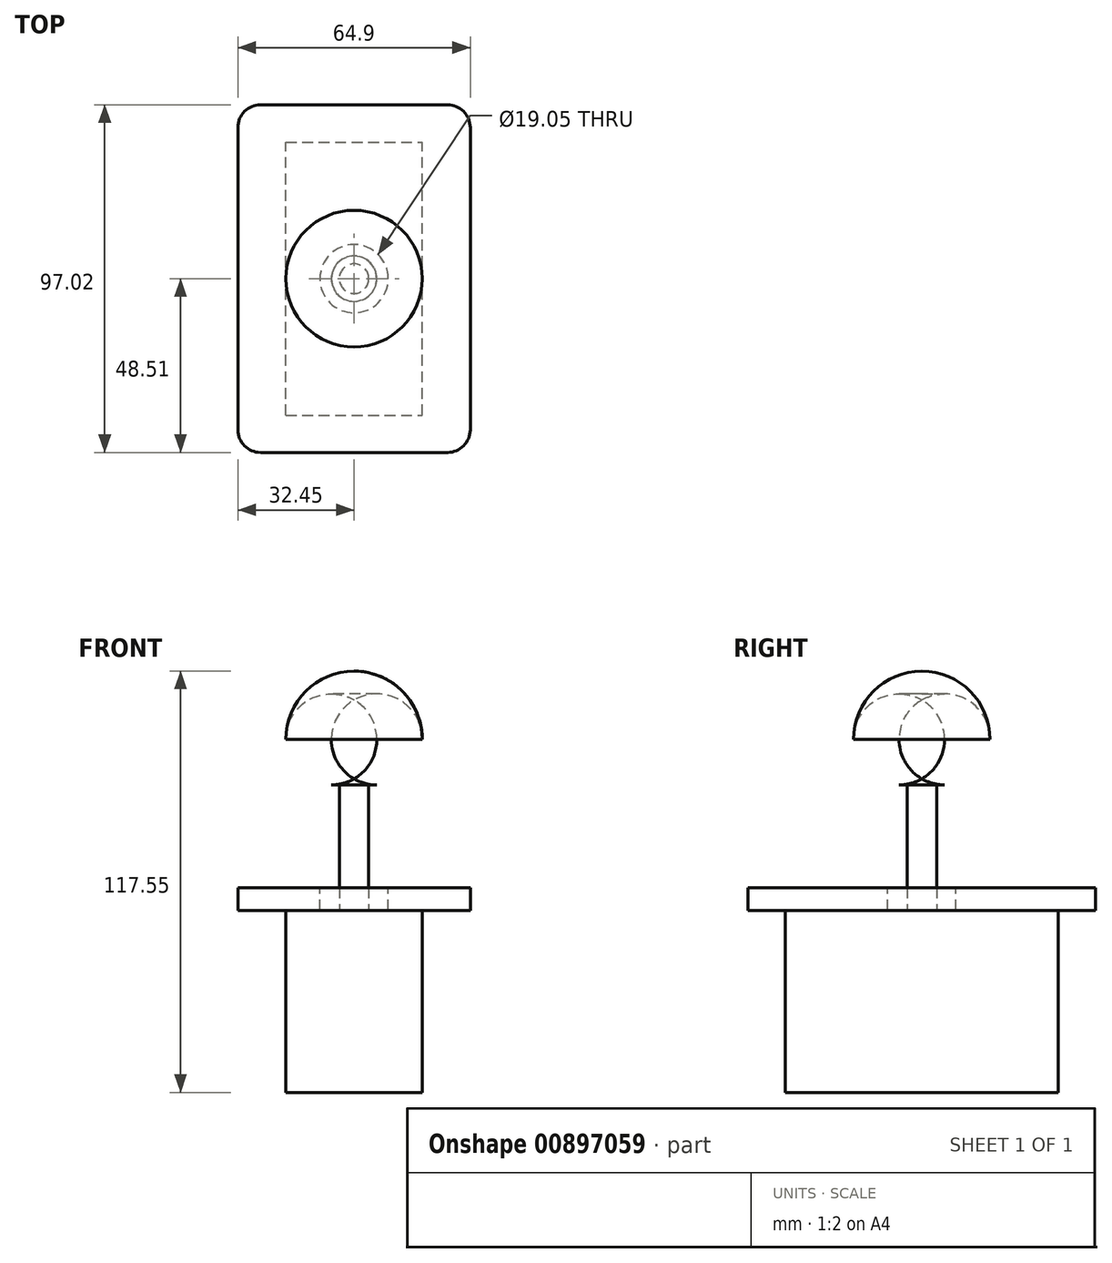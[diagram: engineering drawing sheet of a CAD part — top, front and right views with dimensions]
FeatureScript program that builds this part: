
annotation { "Feature Type Name" : "Feature", "Feature Type Description" : "" }
export const myFeature = defineFeature(function(context is Context, id is Id, definition is map)
    precondition{}
    {
        {
            var Q0;
            Q0=qCreatedBy(makeId("Top.planeOp"),FACE);
            var sketch = newSketch(context, id + "F0", { "sketchPlane" : qUnion([Q0])});
            skCircle(sketch, "E0", {"center": v(0, 0) * mm, "radius": 9.53 * mm});
            skLineSegment(sketch, "E1.bottom", {"start": v(-32.44, 48.5) * mm, "end": v(32.44, 48.5) * mm, "construction": true});
            skLineSegment(sketch, "E1.top", {"start": v(-26.1, -48.5) * mm, "end": v(26.1, -48.5) * mm, "construction": true});
            skLineSegment(sketch, "E1.left", {"start": v(-32.45, 42.16) * mm, "end": v(-32.45, -42.16) * mm, "construction": true});
            skLineSegment(sketch, "E1.right", {"start": v(32.45, 42.16) * mm, "end": v(32.45, -42.16) * mm, "construction": true});
            skPoint(sketch, "E2", {"position": v(0, 48.5) * mm});
            skPoint(sketch, "E3", {"position": v(0, -48.5) * mm});
            skLineSegment(sketch, "E4", {"start": v(0, 48.5) * mm, "end": v(0, -48.5) * mm, "construction": true});
            skLineSegment(sketch, "E5.bottom", {"start": v(-26.1, 48.5) * mm, "end": v(26.1, 48.5) * mm, "construction": true});
            skLineSegment(sketch, "E5.top", {"start": v(-32.44, -48.5) * mm, "end": v(32.45, -48.5) * mm, "construction": true});
            skLineSegment(sketch, "E5.left", {"start": v(-32.44, 48.5) * mm, "end": v(-32.44, -48.5) * mm, "construction": true});
            skLineSegment(sketch, "E5.right", {"start": v(32.45, 48.5) * mm, "end": v(32.45, -48.5) * mm, "construction": true});
            skPoint(sketch, "E6.visualSharp", {"position": v(-32.44, 48.5) * mm});
            skArc(sketch, "E6.filletArc", {"start": v(-26.1, 48.5) * mm, "mid": v(-30.59, 46.65) * mm, "end": v(-32.45, 42.16) * mm});
            skPoint(sketch, "E7.visualSharp", {"position": v(32.45, 48.5) * mm});
            skArc(sketch, "E7.filletArc", {"start": v(32.44, 42.16) * mm, "mid": v(30.59, 46.65) * mm, "end": v(26.1, 48.5) * mm});
            skPoint(sketch, "E8.visualSharp", {"position": v(32.45, -48.5) * mm});
            skArc(sketch, "E8.filletArc", {"start": v(26.1, -48.5) * mm, "mid": v(30.59, -46.65) * mm, "end": v(32.45, -42.16) * mm});
            skPoint(sketch, "E9.visualSharp", {"position": v(-32.45, -48.5) * mm});
            skArc(sketch, "E9.filletArc", {"start": v(-32.45, -42.16) * mm, "mid": v(-30.59, -46.65) * mm, "end": v(-26.1, -48.5) * mm});
            skLineSegment(sketch, "E10", {"start": v(-26.1, 48.5) * mm, "end": v(26.1, 48.5) * mm});
            skLineSegment(sketch, "E11", {"start": v(32.45, 42.16) * mm, "end": v(32.45, -42.16) * mm});
            skLineSegment(sketch, "E12", {"start": v(26.1, -48.5) * mm, "end": v(-26.1, -48.5) * mm});
            skLineSegment(sketch, "E13", {"start": v(-32.45, -42.16) * mm, "end": v(-32.45, 42.16) * mm});
            skSolve(sketch);
        }
        {
            var Q0;
            Q0 = qSketchRegion(id + "F0", true);
            extrude(context, id + "F1", {"entities" : qUnion([Q0]), "oppositeDirection" : true, "depth" : 6.35 * mm, "offsetDistance" : 25.4 * mm});
        }
        {
            var Q0;
            Q0=makeQuery(id+"F1.opExtrude","CAP_FACE",FACE,{"disambiguationData":[OSD([sQuery(id+"F0.wireOp",EDGE,"E0"),sQuery(id+"F0.wireOp",EDGE,"E6.filletArc"),sQuery(id+"F0.wireOp",EDGE,"E7.filletArc"),sQuery(id+"F0.wireOp",EDGE,"E8.filletArc"),sQuery(id+"F0.wireOp",EDGE,"E9.filletArc"),sQuery(id+"F0.wireOp",EDGE,"E10"),sQuery(id+"F0.wireOp",EDGE,"E11"),sQuery(id+"F0.wireOp",EDGE,"E12"),sQuery(id+"F0.wireOp",EDGE,"E13")])],"isStart":false});
            var sketch = newSketch(context, id + "F2", { "sketchPlane" : qUnion([Q0])});
            skCircle(sketch, "E14", {"center": v(0, 0) * mm, "radius": 4.12 * mm});
            skSolve(sketch);
        }
        {
            var Q0;
            Q0 = qSketchRegion(id + "F2", true);
            extrude(context, id + "F3", {"entities" : qUnion([Q0]), "oppositeDirection" : true, "depth" : 35 * mm, "offsetDistance" : 25.4 * mm});
        }
        {
            var Q0;
            Q0=makeQuery(id+"F3.opExtrude","CAP_FACE",FACE,{"disambiguationData":[OSD([sQuery(id+"F2.wireOp",EDGE,"E14")])],"isStart":false});
            var sketch = newSketch(context, id + "F4", { "sketchPlane" : qUnion([Q0])});
            skCircle(sketch, "E15", {"center": v(0, 0) * mm, "radius": 19.05 * mm});
            skSolve(sketch);
        }
        {
            var Q0;
            Q0 = qSketchRegion(id + "F4", true);
            extrude(context, id + "F5", {"entities" : qUnion([Q0]), "operationType" : NewBodyOperationType.ADD, "depth" : 31.75 * mm, "offsetDistance" : 25.4 * mm});
        }
        {
            var Q0;
            Q0=makeQuery(id+"F5.opExtrude","CAP_EDGE",EDGE,{"disambiguationData":[OSD([sQuery(id+"F4.wireOp",EDGE,"E15")])],"isStart":false});
            fillet(context, id + "F6", {"entities" : qUnion([Q0]), "radius" : 19.05 * mm, "tangentPropagation" : true, "allowEdgeOverflow" : false});
        }
        {
            var Q0;
            Q0=makeQuery(id+"F5.opExtrude","CAP_EDGE",EDGE,{"disambiguationData":[OSD([sQuery(id+"F4.wireOp",EDGE,"E15")])],"isStart":true});
            fillet(context, id + "F7", {"entities" : qUnion([Q0]), "radius" : 12.7 * mm, "tangentPropagation" : true, "allowEdgeOverflow" : false});
        }
        {
            var Q0;
            Q0=makeQuery(id+"F1.opExtrude","CAP_FACE",FACE,{"disambiguationData":[OSD([sQuery(id+"F0.wireOp",EDGE,"E0"),sQuery(id+"F0.wireOp",EDGE,"E6.filletArc"),sQuery(id+"F0.wireOp",EDGE,"E7.filletArc"),sQuery(id+"F0.wireOp",EDGE,"E8.filletArc"),sQuery(id+"F0.wireOp",EDGE,"E9.filletArc"),sQuery(id+"F0.wireOp",EDGE,"E10"),sQuery(id+"F0.wireOp",EDGE,"E11"),sQuery(id+"F0.wireOp",EDGE,"E12"),sQuery(id+"F0.wireOp",EDGE,"E13")])],"isStart":false});
            var sketch = newSketch(context, id + "F8", { "sketchPlane" : qUnion([Q0])});
            skLineSegment(sketch, "E16.bottom", {"start": v(-19.05, 38.1) * mm, "end": v(19.05, 38.1) * mm});
            skLineSegment(sketch, "E16.top", {"start": v(-19.05, -38.1) * mm, "end": v(19.05, -38.1) * mm});
            skLineSegment(sketch, "E16.left", {"start": v(-19.05, 38.1) * mm, "end": v(-19.05, -38.1) * mm});
            skLineSegment(sketch, "E16.right", {"start": v(19.05, 38.1) * mm, "end": v(19.05, -38.1) * mm});
            skPoint(sketch, "E17", {"position": v(0, 38.1) * mm});
            skPoint(sketch, "E18", {"position": v(0, -38.1) * mm});
            skLineSegment(sketch, "E19", {"start": v(0, 38.1) * mm, "end": v(0, -38.1) * mm, "construction": true});
            skPoint(sketch, "E20", {"position": v(0, 0) * mm});
            skSolve(sketch);
        }
        {
            var Q0;
            Q0=makeQuery(id+"F8.imprint","IMPRINT",FACE,{"disambiguationData":[TD([[makeQuery(id+"F8.imprint","IMPRINT",EDGE,{"derivedFrom":sQuery(id+"F8.wireOp",EDGE,"E16.bottom")}),-1.0]])]});
            var Q1;
            Q1=makeQuery(id+"F8.imprint","IMPRINT",FACE,{"disambiguationData":[TD([[makeQuery(id+"F8.imprint","IMPRINT",EDGE,{"derivedFrom":makeQuery(id+"F1.opExtrude","CAP_EDGE",EDGE,{"disambiguationData":[OSD([sQuery(id+"F0.wireOp",EDGE,"E0")])],"isStart":false})}),-1.0]])]});
            var Q2;
            Q2=sQuery(id+"F8.wireOp",EDGE,"E19");
            var Q3;
            Q3=sQuery(id+"F8.wireOp",EDGE,"E16.bottom");
            var Q4;
            Q4=sQuery(id+"F8.wireOp",EDGE,"E16.left");
            var Q5;
            Q5=sQuery(id+"F8.wireOp",EDGE,"E16.right");
            var Q6;
            Q6=sQuery(id+"F8.wireOp",EDGE,"E16.top");
            extrude(context, id + "F9", {"entities" : qUnion([Q0, Q1]), "surfaceEntities" : qUnion([Q2, Q3, Q4, Q5, Q6]), "depth" : 50.8 * mm, "offsetDistance" : 25.4 * mm});
        }
    });
